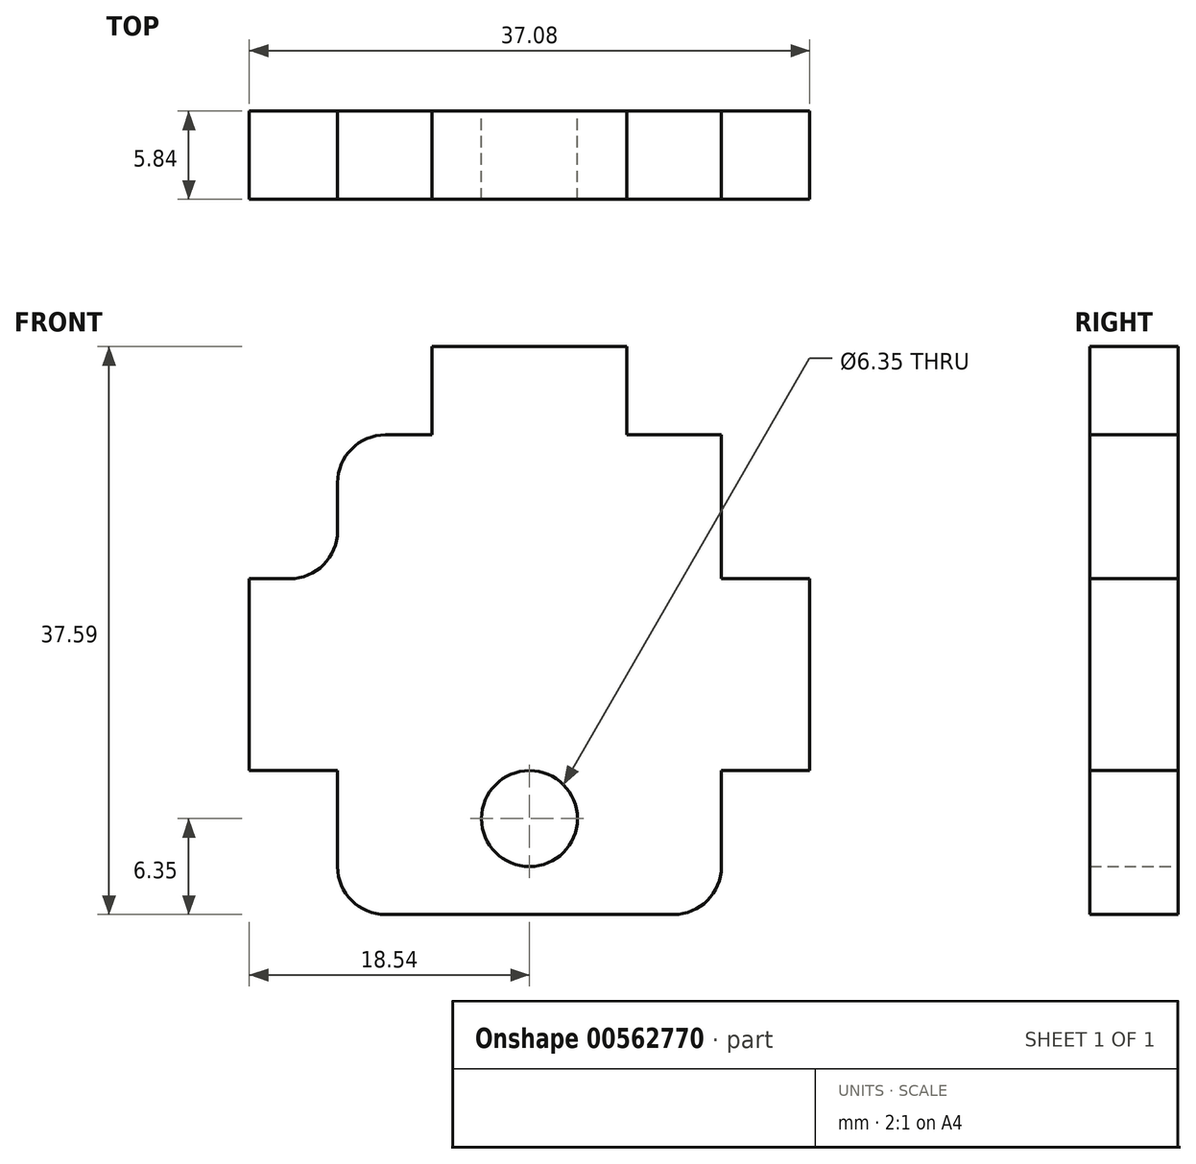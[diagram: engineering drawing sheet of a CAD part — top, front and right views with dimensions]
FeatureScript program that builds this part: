
annotation { "Feature Type Name" : "Feature", "Feature Type Description" : "" }
export const myFeature = defineFeature(function(context is Context, id is Id, definition is map)
    precondition{}
    {
        {
            var Q0;
            Q0=qCreatedBy(makeId("Front.planeOp"),FACE);
            var sketch = newSketch(context, id + "F0", { "sketchPlane" : qUnion([Q0])});
            skCircle(sketch, "E0", {"center": v(0, 0) * mm, "radius": 3.18 * mm});
            skLineSegment(sketch, "E1.top", {"start": v(-12.7, -6.35) * mm, "end": v(12.7, -6.35) * mm});
            skLineSegment(sketch, "E1.left", {"start": v(-12.7, 25.4) * mm, "end": v(-12.7, 15.88) * mm});
            skLineSegment(sketch, "E2", {"start": v(-12.7, 9.53) * mm, "end": v(12.7, 9.53) * mm, "construction": true});
            skLineSegment(sketch, "E3", {"start": v(0, 25.4) * mm, "end": v(0, -6.35) * mm, "construction": true});
            skLineSegment(sketch, "E4.top", {"start": v(-6.45, 31.24) * mm, "end": v(6.45, 31.24) * mm});
            skLineSegment(sketch, "E4.left", {"start": v(-6.45, 25.4) * mm, "end": v(-6.45, 31.24) * mm});
            skLineSegment(sketch, "E4.right", {"start": v(6.45, 25.4) * mm, "end": v(6.45, 31.24) * mm});
            skPoint(sketch, "E4.middle", {"position": v(0, 28.32) * mm});
            skLineSegment(sketch, "E5.trimOffspring", {"start": v(6.45, 25.4) * mm, "end": v(12.7, 25.4) * mm});
            skLineSegment(sketch, "E6", {"start": v(-12.7, 25.4) * mm, "end": v(-6.45, 25.4) * mm});
            skLineSegment(sketch, "E7.bottom", {"start": v(12.7, 15.88) * mm, "end": v(18.54, 15.88) * mm});
            skLineSegment(sketch, "E7.top", {"start": v(12.7, 3.18) * mm, "end": v(18.54, 3.18) * mm});
            skLineSegment(sketch, "E7.right", {"start": v(18.54, 15.88) * mm, "end": v(18.54, 3.18) * mm});
            skPoint(sketch, "E7.middle", {"position": v(15.62, 9.53) * mm});
            skLineSegment(sketch, "E8.trimOffspring", {"start": v(12.7, 3.18) * mm, "end": v(12.7, -6.35) * mm});
            skLineSegment(sketch, "E9", {"start": v(12.7, 15.88) * mm, "end": v(12.7, 25.4) * mm});
            skLineSegment(sketch, "E10.MirrorCS", {"start": v(-12.7, 3.18) * mm, "end": v(-12.7, -6.35) * mm});
            skLineSegment(sketch, "E11.MirrorCS", {"start": v(-12.7, 15.88) * mm, "end": v(-12.7, 25.4) * mm});
            skPoint(sketch, "E12.MirrorP", {"position": v(-15.62, 9.53) * mm});
            skLineSegment(sketch, "E13.MirrorCS", {"start": v(-12.7, 15.88) * mm, "end": v(-18.54, 15.88) * mm});
            skLineSegment(sketch, "E14.MirrorCS", {"start": v(-12.7, 3.18) * mm, "end": v(-18.54, 3.18) * mm});
            skLineSegment(sketch, "E15.MirrorCS", {"start": v(-18.54, 15.88) * mm, "end": v(-18.54, 3.18) * mm});
            skSolve(sketch);
        }
        {
            var Q0;
            Q0 = qSketchRegion(id + "F0", true);
            extrude(context, id + "F1", {"entities" : qUnion([Q0]), "depth" : 5.84 * mm, "offsetDistance" : 25.4 * mm});
        }
        {
            var Q0;
            Q0=makeQuery(id+"F1.opExtrude","SWEPT_EDGE",EDGE,{"disambiguationData":[OSD([sQuery(id+"F0.wireOp",EDGE,"E1.top"),sQuery(id+"F0.wireOp",EDGE,"E1.right")])]});
            var Q1;
            Q1=makeQuery(id+"F1.opExtrude","SWEPT_EDGE",EDGE,{"disambiguationData":[OSD([sQuery(id+"F0.wireOp",EDGE,"E1.top"),sQuery(id+"F0.wireOp",EDGE,"E1.left")])]});
            fillet(context, id + "F2", {"entities" : qUnion([Q0, Q1]), "radius" : 3.17 * mm, "tangentPropagation" : true, "allowEdgeOverflow" : false});
        }
    });
